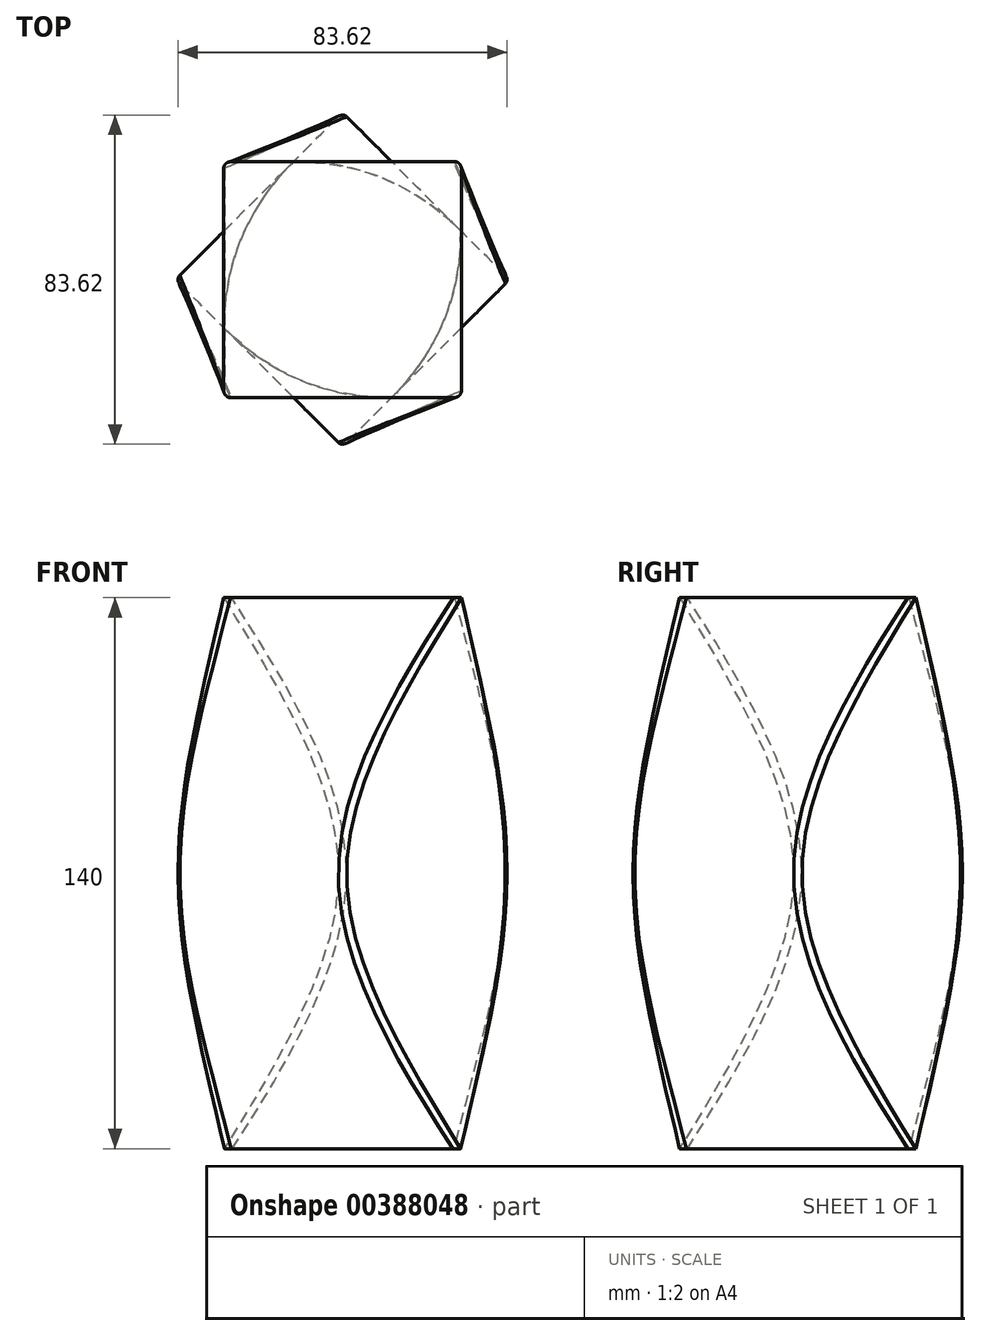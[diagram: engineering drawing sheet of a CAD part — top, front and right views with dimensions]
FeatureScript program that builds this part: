
annotation { "Feature Type Name" : "Feature", "Feature Type Description" : "" }
export const myFeature = defineFeature(function(context is Context, id is Id, definition is map)
    precondition{}
    {
        {
            var Q0;
            Q0=qCreatedBy(makeId("Top.planeOp"),FACE);
            var sketch = newSketch(context, id + "F0", { "sketchPlane" : qUnion([Q0])});
            skLineSegment(sketch, "E0.bottom", {"start": v(30, 30) * mm, "end": v(-30, 30) * mm});
            skLineSegment(sketch, "E0.top", {"start": v(30, -30) * mm, "end": v(-30, -30) * mm});
            skLineSegment(sketch, "E0.left", {"start": v(30, 30) * mm, "end": v(30, -30) * mm});
            skLineSegment(sketch, "E0.right", {"start": v(-30, 30) * mm, "end": v(-30, -30) * mm});
            skPoint(sketch, "E0.middle", {"position": v(0, 0) * mm});
            skSolve(sketch);
        }
        {
            var Q0;
            Q0=qCreatedBy(makeId("Top.planeOp"),FACE);
            cPlane(context, id + "F1", {"entities" : qUnion([Q0]), "cplaneType" : CPlaneType.OFFSET, "offset" : 70 * mm, "width" : 150 * mm, "height" : 150 * mm});
        }
        {
            var Q0;
            Q0=qCreatedBy(id+"F1.planeOp",FACE);
            var sketch = newSketch(context, id + "F2", { "sketchPlane" : qUnion([Q0])});
            skLineSegment(sketch, "E1.bottom", {"start": v(42.43, 0) * mm, "end": v(0, -42.43) * mm});
            skLineSegment(sketch, "E1.top", {"start": v(0, 42.43) * mm, "end": v(-42.43, 0) * mm});
            skLineSegment(sketch, "E1.left", {"start": v(42.43, 0) * mm, "end": v(0, 42.43) * mm});
            skLineSegment(sketch, "E1.right", {"start": v(0, -42.43) * mm, "end": v(-42.43, 0) * mm});
            skPoint(sketch, "E1.middle", {"position": v(0, 0) * mm});
            skSolve(sketch);
        }
        {
            var Q0;
            Q0=qCreatedBy(id+"F1.planeOp",FACE);
            cPlane(context, id + "F3", {"entities" : qUnion([Q0]), "cplaneType" : CPlaneType.OFFSET, "offset" : 70 * mm, "width" : 150 * mm, "height" : 150 * mm});
        }
        {
            var Q0;
            Q0=qCreatedBy(id+"F3.planeOp",FACE);
            var sketch = newSketch(context, id + "F4", { "sketchPlane" : qUnion([Q0])});
            skLineSegment(sketch, "E2.bottom", {"start": v(30.22, -30) * mm, "end": v(-30.22, -30) * mm});
            skLineSegment(sketch, "E2.top", {"start": v(30.22, 30) * mm, "end": v(-30.22, 30) * mm});
            skLineSegment(sketch, "E2.left", {"start": v(30.22, -30) * mm, "end": v(30.22, 30) * mm});
            skLineSegment(sketch, "E2.right", {"start": v(-30.22, -30) * mm, "end": v(-30.22, 30) * mm});
            skPoint(sketch, "E2.middle", {"position": v(0, 0) * mm});
            skSolve(sketch);
        }
        {
            var Q0;
            Q0=makeQuery(id+"F0.imprint","IMPRINT",FACE,{"disambiguationData":[TD([[makeQuery(id+"F0.imprint","IMPRINT",EDGE,{"derivedFrom":sQuery(id+"F0.wireOp",EDGE,"E0.bottom")}),1.0]])]});
            var Q1;
            Q1=makeQuery(id+"F2.imprint","IMPRINT",FACE,{"disambiguationData":[TD([[makeQuery(id+"F2.imprint","IMPRINT",EDGE,{"derivedFrom":sQuery(id+"F2.wireOp",EDGE,"E1.bottom")}),-1.0]])]});
            var Q2;
            Q2=makeQuery(id+"F4.imprint","IMPRINT",FACE,{"disambiguationData":[TD([[makeQuery(id+"F4.imprint","IMPRINT",EDGE,{"derivedFrom":sQuery(id+"F4.wireOp",EDGE,"E2.bottom")}),-1.0]])]});
            loft(context, id + "F5", {"sheetProfilesArray" : [{ "sheetProfileEntities" : qUnion([Q0]) }, { "sheetProfileEntities" : qUnion([Q1]) }, { "sheetProfileEntities" : qUnion([Q2]) }]});
        }
        {
            var Q0;
            Q0=makeQuery(id+"F5.opLoft","SWEPT_EDGE",EDGE,{"disambiguationData":[OSD([sQuery(id+"F0.wireOp",EDGE,"E0.bottom"),sQuery(id+"F0.wireOp",EDGE,"E0.right"),sQuery(id+"F2.wireOp",EDGE,"E1.top"),sQuery(id+"F2.wireOp",EDGE,"E1.right"),sQuery(id+"F4.wireOp",EDGE,"E2.top"),sQuery(id+"F4.wireOp",EDGE,"E2.right")])]});
            var Q1;
            Q1=makeQuery(id+"F5.opLoft","SWEPT_EDGE",EDGE,{"disambiguationData":[OSD([sQuery(id+"F0.wireOp",EDGE,"E0.top"),sQuery(id+"F0.wireOp",EDGE,"E0.right"),sQuery(id+"F2.wireOp",EDGE,"E1.bottom"),sQuery(id+"F2.wireOp",EDGE,"E1.right"),sQuery(id+"F4.wireOp",EDGE,"E2.bottom"),sQuery(id+"F4.wireOp",EDGE,"E2.right")])]});
            var Q2;
            Q2=makeQuery(id+"F5.opLoft","SWEPT_EDGE",EDGE,{"disambiguationData":[OSD([sQuery(id+"F0.wireOp",EDGE,"E0.top"),sQuery(id+"F0.wireOp",EDGE,"E0.left"),sQuery(id+"F2.wireOp",EDGE,"E1.bottom"),sQuery(id+"F2.wireOp",EDGE,"E1.left"),sQuery(id+"F4.wireOp",EDGE,"E2.bottom"),sQuery(id+"F4.wireOp",EDGE,"E2.left")])]});
            var Q3;
            Q3=makeQuery(id+"F5.opLoft","SWEPT_EDGE",EDGE,{"disambiguationData":[OSD([sQuery(id+"F0.wireOp",EDGE,"E0.bottom"),sQuery(id+"F0.wireOp",EDGE,"E0.left"),sQuery(id+"F2.wireOp",EDGE,"E1.top"),sQuery(id+"F2.wireOp",EDGE,"E1.left"),sQuery(id+"F4.wireOp",EDGE,"E2.top"),sQuery(id+"F4.wireOp",EDGE,"E2.left")])]});
            fillet(context, id + "F6", {"entities" : qUnion([Q0, Q1, Q2, Q3]), "radius" : 1.5 * mm, "tangentPropagation" : true, "allowEdgeOverflow" : false});
        }
    });
